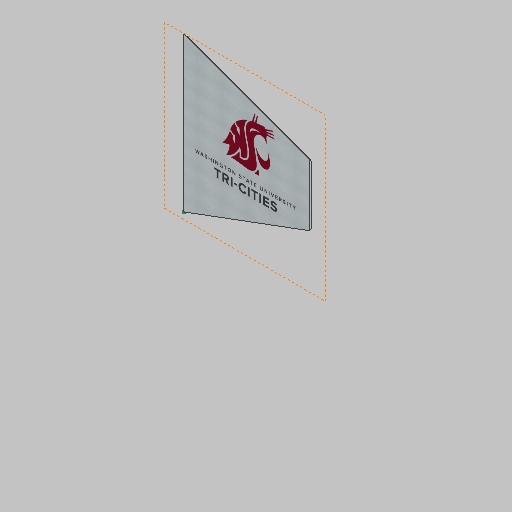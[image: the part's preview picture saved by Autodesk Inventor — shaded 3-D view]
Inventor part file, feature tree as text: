
AUTODESK INVENTOR PART (.ipt)
format: ipt  version: 2023 (Build 270158000, 158)  size: 213,504 bytes
history: native  units: in
note: dims shown in document units (in); Inventor stores cm internally (conversion verified against a paired STEP export)
features: sketch x9, extrude x4, loft x2, plane x2, other x1
ambient origin geometry x8: Origin, YZ Plane, XZ Plane, XY Plane, X Axis, Y Axis, Z Axis, Center Point
bodies: Solid1 (feature_tree)
feature tree (18):
  extrude  "Extrusion1"  Depth=33.0in
  loft  "Loft1"
  loft  "Loft2"
  plane  "Work Plane1"
  plane  "Work Plane2"
  extrude  "Extrusion3"  TaperAngle=135.0deg  [1 undecoded]
  extrude  "Extrusion4"  TaperAngle=0.0deg  [1 undecoded]
  extrude  "Extrusion6"  Depth=0.2947in
  sketch  "Sketch12"  dims[d18=0.0in d19=90.0deg d20=0.1554in d25=16.5in d26=0.469in d27=6.5in d28=0.0in d30=16.414in d31=0.0in d32=0.7661in d37=0.2295in d38=1.0in d39=1.0in d40=0.0in d41=0.0in]
  sketch  "Sketch1"  dims[d0=27.0in d1=33.0in]
  sketch  "Sketch2"  dims[d2=4.0in d3=13.0in]
  sketch  "Sketch3"  dims[d4=10.0in d5=0.5in d6=0.0in]
  sketch  "Sketch4"  dims[d7=0.9422in d8=135.0deg]
  sketch  "Sketch5"  dims[d9=0.2947in d10=0.0in d11=90.0deg]
  sketch  "Sketch7"  dims[d12=0.0in d13=90.0deg d14=0.2947in]
  sketch  "Sketch8"  dims[d15=0.9422in]
  sketch  "Sketch10"  dims[d16=0.0in d17=90.0deg]
  other  "Image1"
note: 2 required parameter values undecoded (feature->parameter linkage not recoverable at this tier; creation-order binding heuristic only, values carry confidence <= 0.55)
